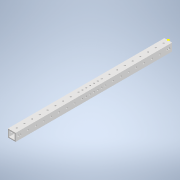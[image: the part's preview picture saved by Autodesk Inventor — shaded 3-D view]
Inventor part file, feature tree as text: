
AUTODESK INVENTOR PART (.ipt)
format: ipt  version: 2020 (Build 240168000, 168)  size: 259,072 bytes
history: native  units: in
note: dims shown in document units (in); Inventor stores cm internally (conversion verified against a paired STEP export)
features: sketch x7, other x7, extrude x6, reference x2
ambient origin geometry x8: Origin, YZ Plane, XZ Plane, XY Plane, X Axis, Y Axis, Z Axis, Center Point
bodies: Solid1 (feature_tree)
feature tree (22):
  extrude  "Extrusion1"  Depth=1.0in
  extrude  "Extrusion2"  Depth=20.25in TaperAngle=0.0deg
  extrude  "Extrusion3"  Depth=0.625in
  sketch  "Sketch4"  dims[d7=0.2in d8=7.874in d10=1.0in d11=0.3937in d13=1.0in]
  extrude  "Extrusion4"  Depth=1.0in
  extrude  "Extrusion5"  Depth=0.5in
  extrude  "Extrusion6"  Depth=0.625in
  sketch  "Sketch1"  dims[d0=1.0in d1=1.0in]
  sketch  "Sketch2"  dims[d2=0.125in d3=20.25in d4=0.0in]
  sketch  "Sketch3"  dims[d5=0.5in d6=0.625in]
  sketch  "Sketch5"  dims[d15=0.0in d16=0.0in d17=0.5in]
  reference  "Reference1"
  reference  "Reference2"
  sketch  "Sketch6"  dims[d18=0.625in d19=0.2in]
  sketch  "Sketch8"  dims[d20=7.874in d22=1.0in d23=0.3937in d25=1.0in d27=0.0in d28=0.0in d29=0.0in d30=0.0in d31=10.125in d32=1.5in d33=1.1811in d35=1.0in d36=0.3937in d38=1.0in d40=0.0in d41=0.0in d42=0.5in d43=1.1811in d45=1.0in d46=0.3937in d48=1.0in d50=0.0in d51=0.0in]
  other  "<userpath>\Documents\FRC\2020\Prototype1.iam"
  other  "Prototype1.iam"
  other  "DriveBase2020:1"
  other  "AM14U3 Long Half_1"
  other  "AM14U3 Long Frame Half_3"
  other  "AM14U3 Inside Sheet Rev2_136"
  other  "AM14U3 Long Half:2"
